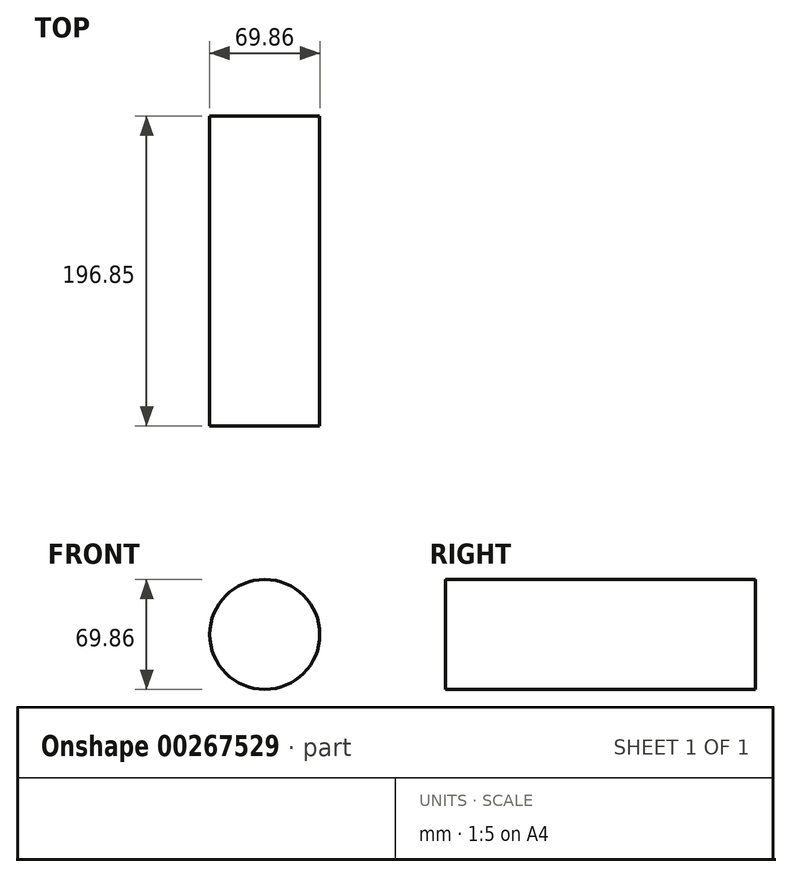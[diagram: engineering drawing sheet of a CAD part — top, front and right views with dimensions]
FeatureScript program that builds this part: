
annotation { "Feature Type Name" : "Feature", "Feature Type Description" : "" }
export const myFeature = defineFeature(function(context is Context, id is Id, definition is map)
    precondition{}
    {
        {
            var Q0;
            Q0=qCreatedBy(makeId("Front.planeOp"),FACE);
            var sketch = newSketch(context, id + "F0", { "sketchPlane" : qUnion([Q0])});
            skCircle(sketch, "E0", {"center": v(0, 0) * mm, "radius": 34.93 * mm});
            skSolve(sketch);
        }
        {
            var Q0;
            Q0=sQuery(id+"F0.wireOp",EDGE,"E0");
            extrude(context, id + "F1", {"bodyType" : ToolBodyType.SURFACE, "surfaceEntities" : qUnion([Q0]), "depth" : 196.85 * mm});
        }
    });
